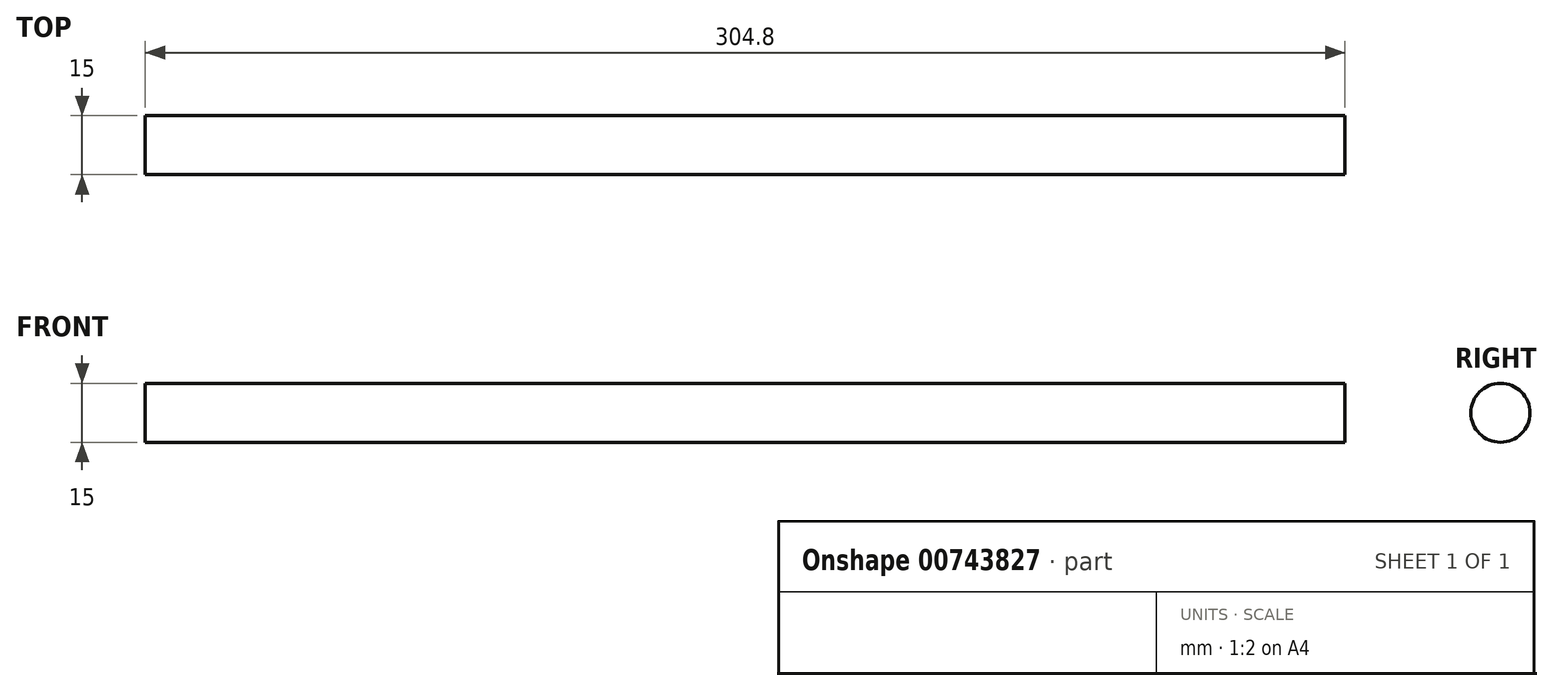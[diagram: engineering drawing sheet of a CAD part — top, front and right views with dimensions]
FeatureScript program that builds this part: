
annotation { "Feature Type Name" : "Feature", "Feature Type Description" : "" }
export const myFeature = defineFeature(function(context is Context, id is Id, definition is map)
    precondition{}
    {
        {
            var Q0;
            Q0=qCreatedBy(makeId("Right.planeOp"),FACE);
            var sketch = newSketch(context, id + "F0", { "sketchPlane" : qUnion([Q0])});
            skCircle(sketch, "E0", {"center": v(0, 0) * mm, "radius": 7.5 * mm});
            skSolve(sketch);
        }
        {
            var Q0;
            Q0=makeQuery(id+"F0.imprint","IMPRINT",FACE,{"disambiguationData":[TD([[makeQuery(id+"F0.imprint","IMPRINT",EDGE,{"derivedFrom":sQuery(id+"F0.wireOp",EDGE,"E0")}),1.0]])]});
            extrude(context, id + "F1", {"entities" : qUnion([Q0]), "endBound" : BoundingType.SYMMETRIC, "depth" : 304.8 * mm, "offsetDistance" : 25.4 * mm});
        }
    });
